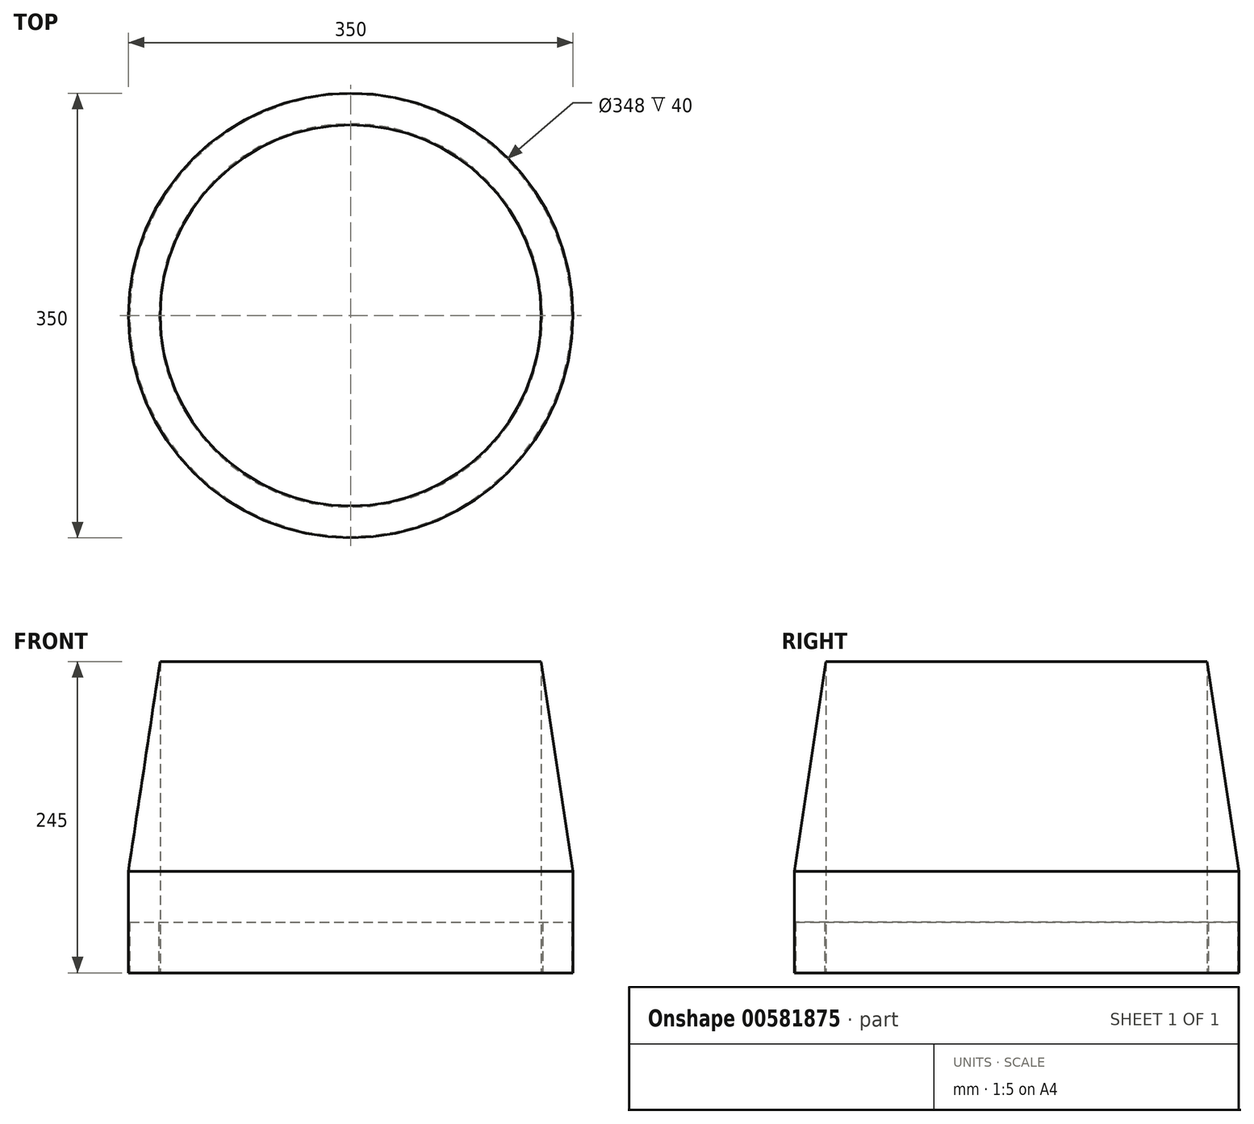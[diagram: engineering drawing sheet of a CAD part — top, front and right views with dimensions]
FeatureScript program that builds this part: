
annotation { "Feature Type Name" : "Feature", "Feature Type Description" : "" }
export const myFeature = defineFeature(function(context is Context, id is Id, definition is map)
    precondition{}
    {
        {
            var Q0;
            Q0=qCreatedBy(makeId("Front.planeOp"),FACE);
            var sketch = newSketch(context, id + "F0", { "sketchPlane" : qUnion([Q0])});
            skLineSegment(sketch, "E0", {"start": v(0, -139.25) * mm, "end": v(0, 240.83) * mm, "construction": true});
            skLineSegment(sketch, "E1", {"start": v(-150, -67.22) * mm, "end": v(-150, 177.78) * mm});
            skLineSegment(sketch, "E2", {"start": v(-150, 177.78) * mm, "end": v(-175, 12.78) * mm});
            skLineSegment(sketch, "E3", {"start": v(-175, 12.78) * mm, "end": v(-175, -67.22) * mm});
            skLineSegment(sketch, "E4", {"start": v(-175, -67.22) * mm, "end": v(-174, -67.22) * mm});
            skLineSegment(sketch, "E5", {"start": v(-174, -67.22) * mm, "end": v(-174, -27.22) * mm});
            skLineSegment(sketch, "E6", {"start": v(-174, -27.22) * mm, "end": v(-151, -27.22) * mm});
            skLineSegment(sketch, "E7", {"start": v(-151, -27.22) * mm, "end": v(-151, -67.22) * mm});
            skLineSegment(sketch, "E8", {"start": v(-151, -67.22) * mm, "end": v(-150, -67.22) * mm});
            skSolve(sketch);
        }
        {
            var Q0;
            Q0=qSketchRegion(id+"F0",true);
            var Q1;
            Q1=sQuery(id+"F0.wireOp",EDGE,"E0");
            revolve(context, id + "F1", {"entities" : qUnion([Q0]), "axis" : qUnion([Q1]), "revolveType" : RevolveType.FULL});
        }
    });
